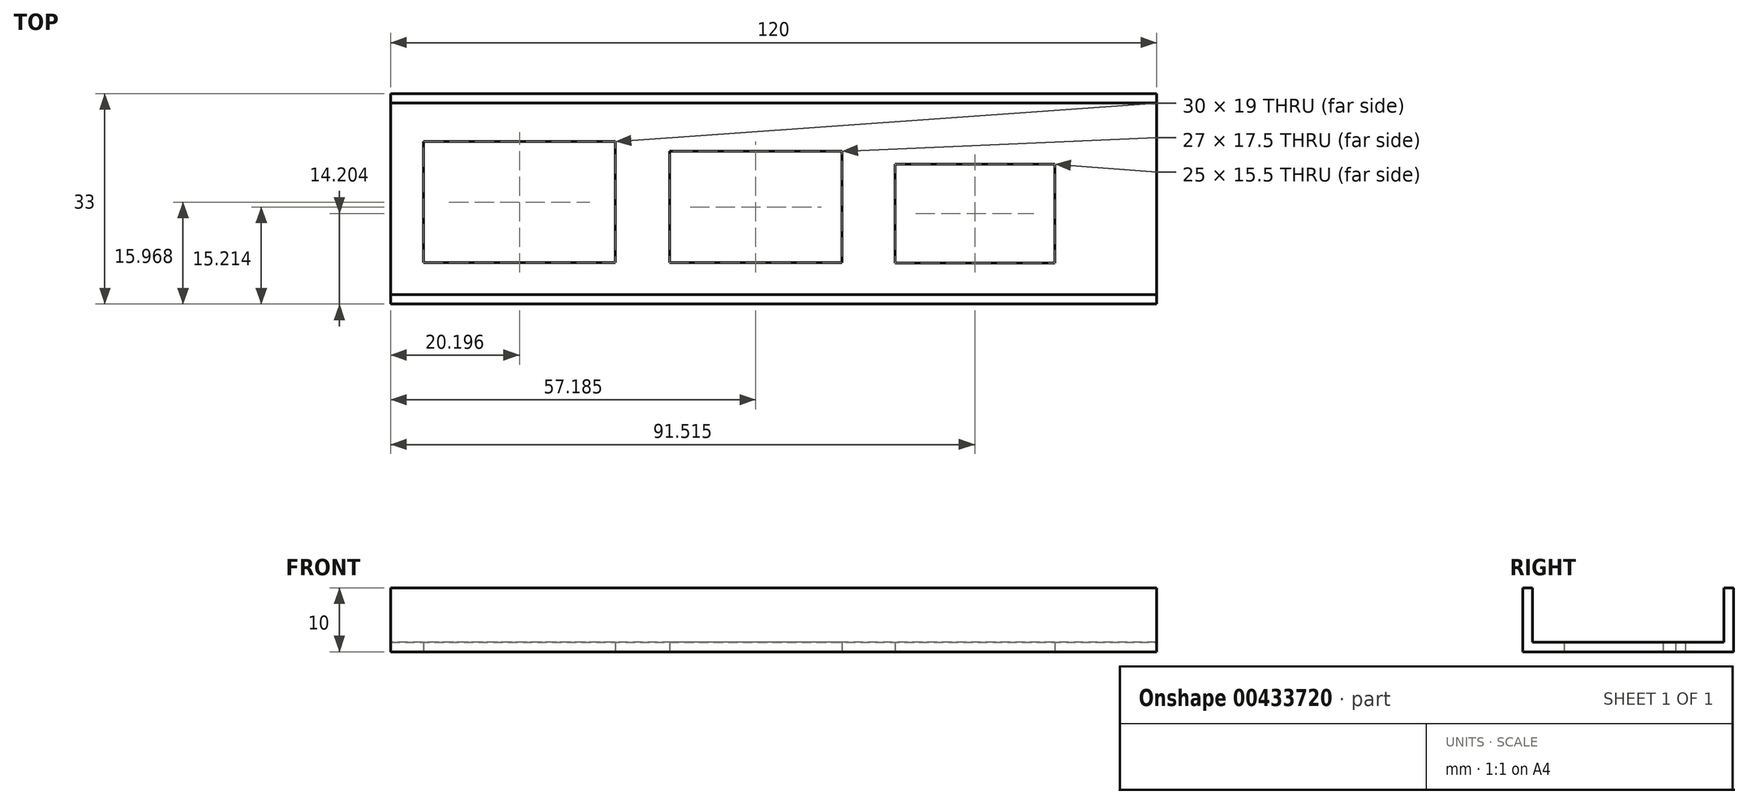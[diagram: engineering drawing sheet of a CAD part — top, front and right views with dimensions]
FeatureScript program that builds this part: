
annotation { "Feature Type Name" : "Feature", "Feature Type Description" : "" }
export const myFeature = defineFeature(function(context is Context, id is Id, definition is map)
    precondition{}
    {
        {
            var Q0;
            Q0=qCreatedBy(makeId("Top.planeOp"),FACE);
            var sketch = newSketch(context, id + "F0", { "sketchPlane" : qUnion([Q0])});
            skLineSegment(sketch, "E0.bottom", {"start": v(60, -15) * mm, "end": v(-60, -15) * mm});
            skLineSegment(sketch, "E0.top", {"start": v(60, 15) * mm, "end": v(-60, 15) * mm});
            skLineSegment(sketch, "E0.left", {"start": v(60, -15) * mm, "end": v(60, 15) * mm});
            skLineSegment(sketch, "E0.right", {"start": v(-60, -15) * mm, "end": v(-60, 15) * mm});
            skPoint(sketch, "E0.middle", {"position": v(0, 0) * mm});
            skLineSegment(sketch, "E1.bottom", {"start": v(44.02, -10.05) * mm, "end": v(19.02, -10.05) * mm});
            skLineSegment(sketch, "E1.top", {"start": v(44.02, 5.45) * mm, "end": v(19.02, 5.45) * mm});
            skLineSegment(sketch, "E1.left", {"start": v(44.02, -10.05) * mm, "end": v(44.02, 5.45) * mm});
            skLineSegment(sketch, "E1.right", {"start": v(19.02, -10.05) * mm, "end": v(19.02, 5.45) * mm});
            skPoint(sketch, "E1.middle", {"position": v(31.52, -2.3) * mm});
            skPoint(sketch, "E2.middle", {"position": v(0.54, -12.52) * mm});
            skLineSegment(sketch, "E3.bottom", {"start": v(10.68, -10.04) * mm, "end": v(-16.32, -10.04) * mm});
            skLineSegment(sketch, "E3.top", {"start": v(10.68, 7.46) * mm, "end": v(-16.32, 7.46) * mm});
            skLineSegment(sketch, "E3.left", {"start": v(10.68, -10.04) * mm, "end": v(10.68, 7.46) * mm});
            skLineSegment(sketch, "E3.right", {"start": v(-16.32, -10.04) * mm, "end": v(-16.32, 7.46) * mm});
            skPoint(sketch, "E3.middle", {"position": v(-2.82, -1.29) * mm});
            skLineSegment(sketch, "E4.bottom", {"start": v(-24.8, -10.03) * mm, "end": v(-54.8, -10.03) * mm});
            skLineSegment(sketch, "E4.top", {"start": v(-24.8, 8.97) * mm, "end": v(-54.8, 8.97) * mm});
            skLineSegment(sketch, "E4.left", {"start": v(-24.8, -10.03) * mm, "end": v(-24.8, 8.97) * mm});
            skLineSegment(sketch, "E4.right", {"start": v(-54.8, -10.03) * mm, "end": v(-54.8, 8.97) * mm});
            skPoint(sketch, "E4.middle", {"position": v(-39.8, -0.53) * mm});
            skSolve(sketch);
        }
        {
            var Q0;
            Q0=makeQuery(id+"F0.imprint","IMPRINT",FACE,{"disambiguationData":[TD([[makeQuery(id+"F0.imprint","IMPRINT",EDGE,{"derivedFrom":sQuery(id+"F0.wireOp",EDGE,"E0.bottom")}),-1.0]])]});
            extrude(context, id + "F1", {"entities" : qUnion([Q0]), "depth" : 1.5 * mm, "offsetDistance" : 25.4 * mm});
        }
        {
            var Q0;
            Q0=qCreatedBy(makeId("Top.planeOp"),FACE);
            var sketch = newSketch(context, id + "F2", { "sketchPlane" : qUnion([Q0])});
            skLineSegment(sketch, "E5.bottom", {"start": v(-60, 15) * mm, "end": v(60, 15) * mm});
            skLineSegment(sketch, "E5.top", {"start": v(-60, 16.5) * mm, "end": v(60, 16.5) * mm});
            skLineSegment(sketch, "E5.left", {"start": v(-60, 15) * mm, "end": v(-60, 16.5) * mm});
            skLineSegment(sketch, "E5.right", {"start": v(60, 15) * mm, "end": v(60, 16.5) * mm});
            skLineSegment(sketch, "E6.bottom", {"start": v(-60, -15) * mm, "end": v(60, -15) * mm});
            skLineSegment(sketch, "E6.top", {"start": v(-60, -16.5) * mm, "end": v(60, -16.5) * mm});
            skLineSegment(sketch, "E6.left", {"start": v(-60, -15) * mm, "end": v(-60, -16.5) * mm});
            skLineSegment(sketch, "E6.right", {"start": v(60, -15) * mm, "end": v(60, -16.5) * mm});
            skSolve(sketch);
        }
        {
            var Q0;
            Q0 = qSketchRegion(id + "F2", true);
            extrude(context, id + "F3", {"entities" : qUnion([Q0]), "operationType" : NewBodyOperationType.ADD, "depth" : 10 * mm, "offsetDistance" : 25.4 * mm});
        }
    });
